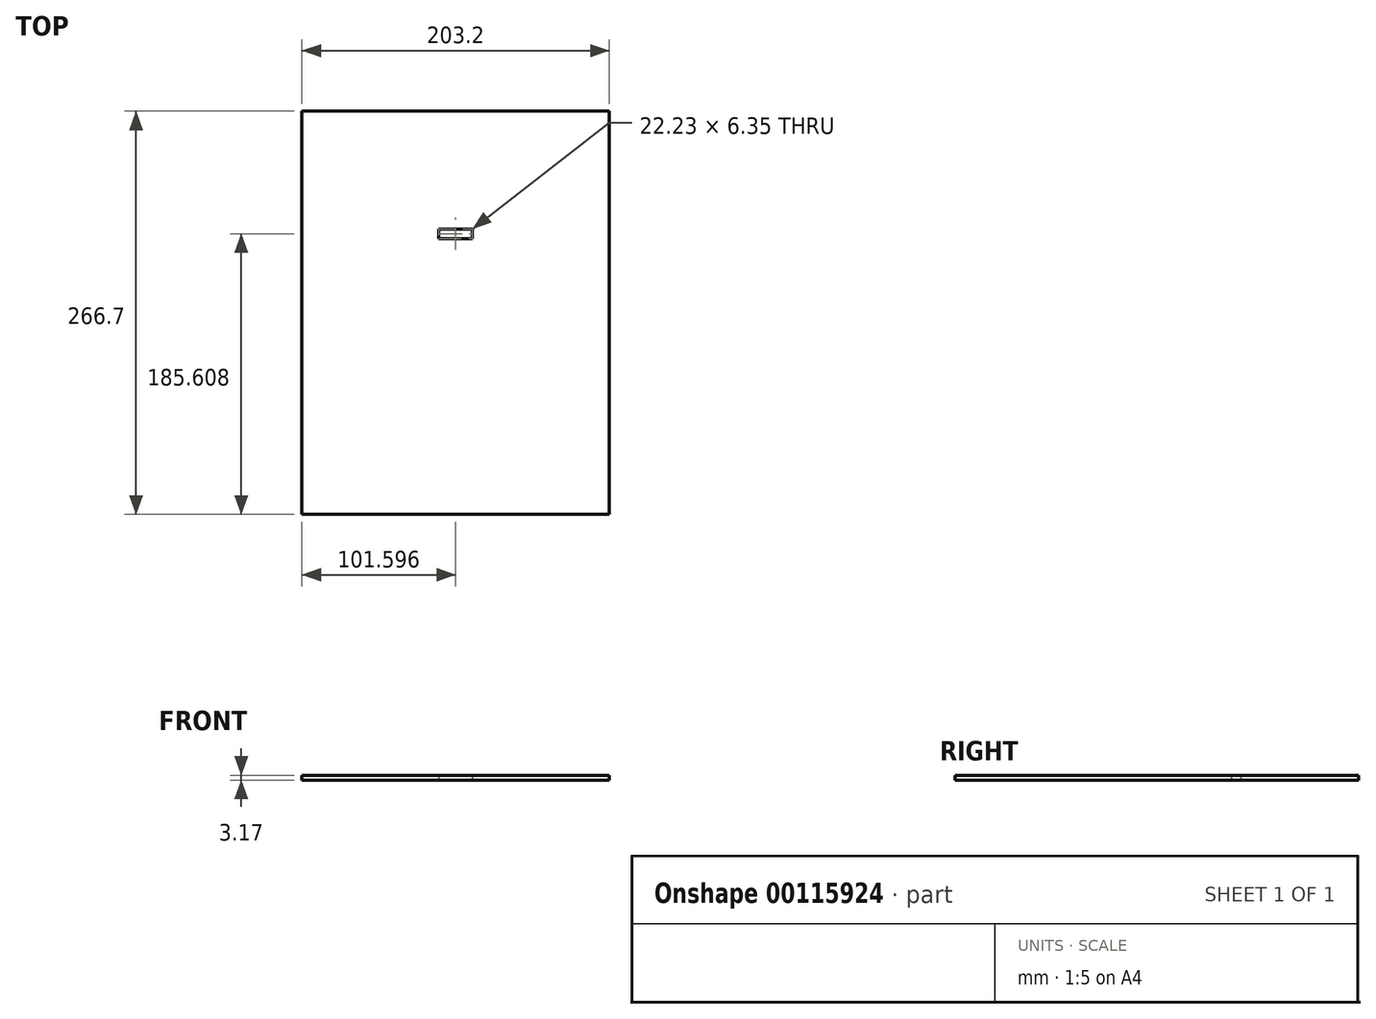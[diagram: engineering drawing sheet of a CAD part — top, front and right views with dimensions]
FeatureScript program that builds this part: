
annotation { "Feature Type Name" : "Feature", "Feature Type Description" : "" }
export const myFeature = defineFeature(function(context is Context, id is Id, definition is map)
    precondition{}
    {
        {
            var Q0;
            Q0=qCreatedBy(makeId("Top.planeOp"),FACE);
            var sketch = newSketch(context, id + "F0", { "sketchPlane" : qUnion([Q0])});
            skLineSegment(sketch, "E0.bottom", {"start": v(-101.34, 171.29) * mm, "end": v(101.86, 171.29) * mm});
            skLineSegment(sketch, "E0.top", {"start": v(-101.34, -95.41) * mm, "end": v(101.86, -95.41) * mm});
            skLineSegment(sketch, "E0.left", {"start": v(-101.34, 171.29) * mm, "end": v(-101.34, -95.41) * mm});
            skLineSegment(sketch, "E0.right", {"start": v(101.86, 171.29) * mm, "end": v(101.86, -95.41) * mm});
            skLineSegment(sketch, "E1.bottom", {"start": v(-10.86, 93.37) * mm, "end": v(11.37, 93.37) * mm});
            skLineSegment(sketch, "E1.top", {"start": v(-10.86, 87.02) * mm, "end": v(11.37, 87.02) * mm});
            skLineSegment(sketch, "E1.left", {"start": v(-10.86, 93.37) * mm, "end": v(-10.86, 87.02) * mm});
            skLineSegment(sketch, "E1.right", {"start": v(11.37, 93.37) * mm, "end": v(11.37, 87.02) * mm});
            skSolve(sketch);
        }
        {
            var Q0;
            Q0=makeQuery(id+"F0.imprint","IMPRINT",FACE,{"disambiguationData":[TD([[makeQuery(id+"F0.imprint","IMPRINT",EDGE,{"derivedFrom":sQuery(id+"F0.wireOp",EDGE,"E0.bottom")}),-1.0]])]});
            extrude(context, id + "F1", {"entities" : qUnion([Q0]), "depth" : 3.17 * mm});
        }
    });
